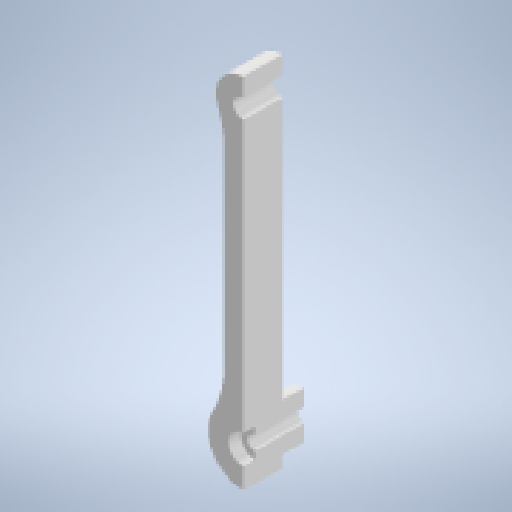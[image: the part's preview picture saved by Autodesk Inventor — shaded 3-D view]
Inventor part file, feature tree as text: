
AUTODESK INVENTOR PART (.ipt)
format: ipt  version: 2025.1 (Build 291241000, 241)  size: 343,552 bytes
history: native  units: mm
features: extrude x6, sketch x5, fillet x4
ambient origin geometry x8: Origin, YZ Plane, XZ Plane, XY Plane, X Axis, Y Axis, Z Axis, Center Point
bodies: Volumenkörper1 (feature_tree)
feature tree (15):
  sketch  "Skizze1"  dims[d2=18.0mm d4=25.0mm]
  extrude  "Extrusion1"  Depth=25.0mm
  extrude  "Extrusion5"  TaperAngle=0.0deg  [1 undecoded]
  fillet  "Rundung3"  Radius=5.0mm
  fillet  "Rundung4"  Radius=5.0mm
  extrude  "Extrusion6"  Depth=5.5mm TaperAngle=0.0deg
  extrude  "Extrusion7"  Depth=0.2mm
  fillet  "Rundung5"  Radius=7.3mm
  fillet  "Rundung6"  Radius=3.0mm
  extrude  "Extrusion8"  Depth=3.0mm TaperAngle=0.0deg
  extrude  "Extrusion9"  Depth=0.2mm
  sketch  "Skizze8"  dims[d6=10.0mm d7=0.0mm d10=0.0mm d33=5.0mm d34=5.0mm]
  sketch  "Skizze10"  dims[d36=12.0mm d37=5.5mm d38=0.0mm]
  sketch  "Skizze11"  dims[d39=0.2mm d40=0.2mm d41=7.3mm d42=3.0mm d43=0.0mm]
  sketch  "Skizze12"  dims[d44=3.5mm d45=3.0mm d46=0.0mm d47=0.2mm d48=0.2mm d49=75.0mm d51=5.0mm d52=9.0mm d53=0.0mm d54=14.0mm d56=10.0mm d57=0.0mm]
note: 1 required parameter value undecoded (feature->parameter linkage not recoverable at this tier; creation-order binding heuristic only, values carry confidence <= 0.55)
